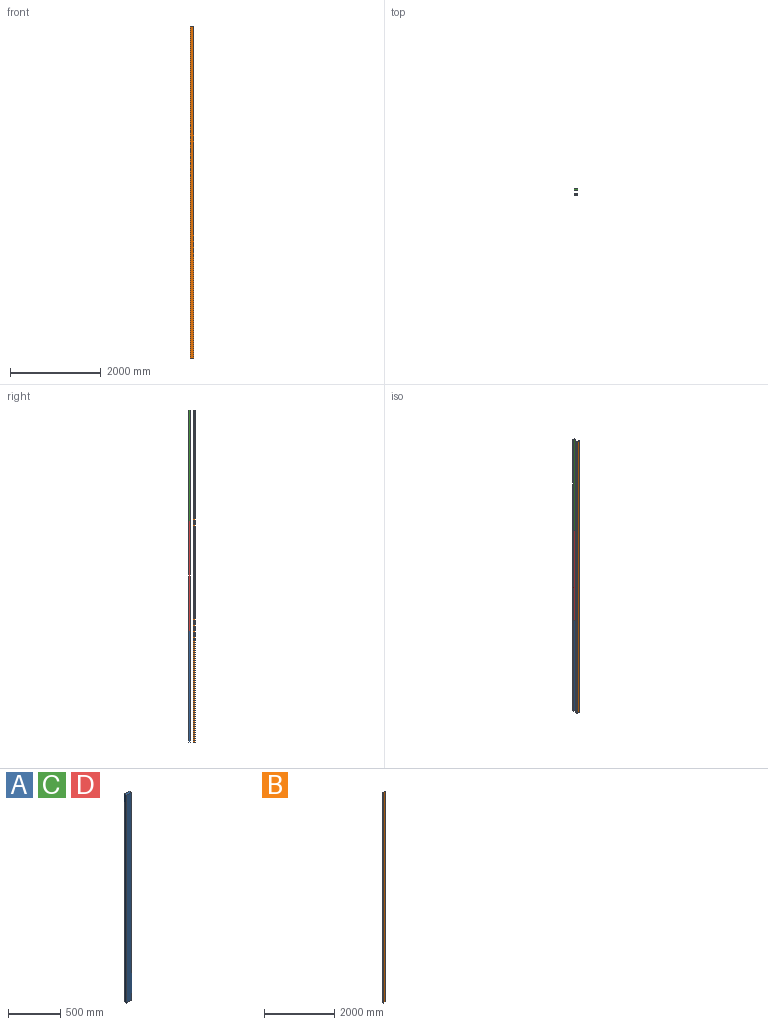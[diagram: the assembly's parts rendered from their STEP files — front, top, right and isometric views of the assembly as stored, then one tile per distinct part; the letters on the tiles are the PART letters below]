
ASSEMBLY  parts=4 mates=3
PART A: 6 faces, bbox 69.9x31.8x2438.4 mm
  f0: plane 2438.4x69.85mm, normal (0,-1,0), area 170322.2mm2, adj f1,f3,f4,f5
  f1: plane 2438.4x31.75mm, normal (1,0,0), area 77419.2mm2, adj f0,f2,f4,f5
  f2: plane 2438.4x69.85mm, normal (0,1,0), area 170322.2mm2, adj f1,f3,f4,f5
  f3: plane 2438.4x31.75mm, normal (-1,0,0), area 77419.2mm2, adj f0,f2,f4,f5
  f4: plane 69.85x31.75mm, normal (0,0,1), area 2217.7mm2, adj f0,f1,f2,f3
  f5: plane 69.85x31.75mm, normal (0,0,-1), area 2217.7mm2, adj f0,f1,f2,f3
PART B: 18 faces, bbox 76.2x38.1x7315.2 mm
  f0: plane 7315.2x31.75mm, normal (1,0,0), area 232257.6mm2, adj f1,f15,f16,f17
  f1: cylinder r=3.17mm len=7315.2mm, axis (0,0,-1), area 36482.9mm2, adj f0,f2,f16,f17
  f2: plane 7315.2x69.85mm, normal (0,1,0), area 510966.7mm2, adj f1,f3,f16,f17
  f3: cylinder r=3.17mm len=7315.2mm, axis (0,0,-1), area 36482.9mm2, adj f2,f4,f16,f17
  f4: plane 7315.2x31.75mm, normal (-1,0,0), area 232257.6mm2, adj f3,f5,f16,f17
  f5: cylinder r=3.17mm len=7315.2mm, axis (0,0,-1), area 36482.9mm2, adj f4,f6,f16,f17
  f6: plane 7315.2x69.85mm, normal (0,-1,0), area 510966.7mm2, adj f5,f15,f16,f17
  f7: cylinder r=3.17mm len=7315.2mm, axis (0,0,-1), area 36482.9mm2, adj f8,f14,f16,f17
  f8: plane 7315.2x66.7mm, normal (0,-1,0), area 487926.8mm2, adj f7,f9,f16,f17
  f9: cylinder r=3.17mm len=7315.2mm, axis (0,0,-1), area 36482.9mm2, adj f8,f10,f16,f17
  f10: plane 7315.2x28.6mm, normal (-1,0,0), area 209217.6mm2, adj f9,f11,f16,f17
  f11: cylinder r=3.17mm len=7315.2mm, axis (0,0,-1), area 36482.9mm2, adj f10,f12,f16,f17
  f12: plane 7315.2x66.7mm, normal (0,1,0), area 487926.8mm2, adj f11,f13,f16,f17
  f13: cylinder r=3.17mm len=7315.2mm, axis (0,0,-1), area 36482.9mm2, adj f12,f14,f16,f17
  f14: plane 7315.2x28.6mm, normal (1,0,0), area 209217.6mm2, adj f7,f13,f16,f17
  f15: cylinder r=3.17mm len=7315.2mm, axis (0,0,-1), area 36482.9mm2, adj f0,f6,f16,f17
  f16: plane 76.2x38.1mm, normal (0,0,1), area 350.1mm2, adj f0,f1,f2,f3,f4,f5,f6,f7
  f17: plane 76.2x38.1mm, normal (0,0,-1), area 350.1mm2, adj f0,f1,f2,f3,f4,f5,f6,f7
PART C: same geometry as A
PART D: same geometry as A
PLACE A t=(-3146.93,86.97,-2769.36)mm
PLACE B t=(-3185.03,-34.17,-2769.36)mm
PLACE C t=(-3146.93,86.97,2107.44)mm
PLACE D t=(-3146.93,86.97,-330.96)mm
MATE fastened A.f4 <-> D.f5  axis (0,0,1) through (-3146.93,86.97,-330.96)mm
MATE fastened D.f4 <-> C.f5  axis (0,0,1) through (-3146.93,86.97,2107.44)mm
MATE slider B.f8 <-> D.f2  axis (0,-1,0) through (-3146.93,2.36,888.24)mm
